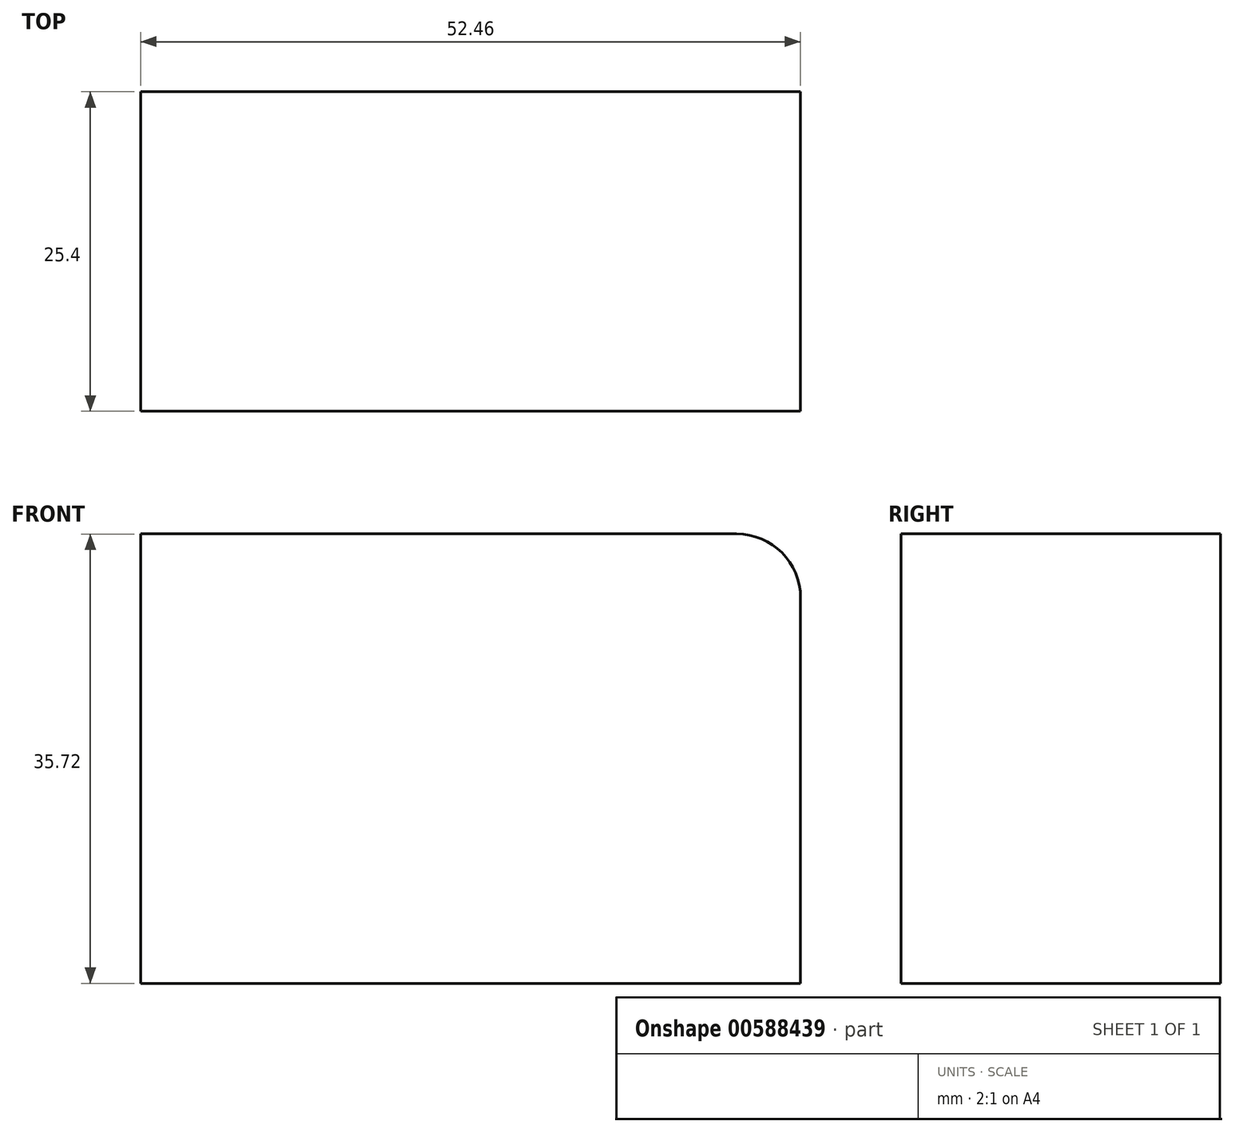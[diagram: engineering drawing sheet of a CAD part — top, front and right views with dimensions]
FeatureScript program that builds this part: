
annotation { "Feature Type Name" : "Feature", "Feature Type Description" : "" }
export const myFeature = defineFeature(function(context is Context, id is Id, definition is map)
    precondition{}
    {
        {
            var Q0;
            Q0=qCreatedBy(makeId("Front.planeOp"),FACE);
            var sketch = newSketch(context, id + "F0", { "sketchPlane" : qUnion([Q0])});
            skLineSegment(sketch, "E0", {"start": v(-61.77, 45.7) * mm, "end": v(-61.77, 9.97) * mm});
            skLineSegment(sketch, "E1", {"start": v(-61.77, 9.97) * mm, "end": v(-9.3, 9.97) * mm});
            skLineSegment(sketch, "E2", {"start": v(-9.3, 9.97) * mm, "end": v(-9.3, 45.7) * mm});
            skLineSegment(sketch, "E3", {"start": v(-9.3, 45.7) * mm, "end": v(-61.77, 45.7) * mm});
            skSolve(sketch);
        }
        {
            var Q0;
            Q0=makeQuery(id+"F0.imprint","IMPRINT",FACE,{"disambiguationData":[TD([[makeQuery(id+"F0.imprint","IMPRINT",EDGE,{"derivedFrom":sQuery(id+"F0.wireOp",EDGE,"E0")}),1.0]])]});
            var sketch = newSketch(context, id + "F1", { "sketchPlane" : qUnion([Q0])});
            skSolve(sketch);
        }
        {
            var Q0;
            Q0 = qSketchRegion(id + "F1", true);
            var Q1;
            Q1=makeQuery(id+"F0.imprint","IMPRINT",FACE,{"disambiguationData":[TD([[makeQuery(id+"F0.imprint","IMPRINT",EDGE,{"derivedFrom":sQuery(id+"F0.wireOp",EDGE,"E0")}),1.0]])]});
            extrude(context, id + "F2", {"entities" : qUnion([Q0, Q1]), "depth" : 25.4 * mm, "offsetDistance" : 25.4 * mm});
        }
        {
            var Q0;
            Q0=makeQuery(id+"F2.opExtrude","SWEPT_EDGE",EDGE,{"disambiguationData":[OSD([sQuery(id+"F0.wireOp",EDGE,"E2"),sQuery(id+"F0.wireOp",EDGE,"E3")])]});
            fillet(context, id + "F3", {"entities" : qUnion([Q0]), "radius" : 5.08 * mm, "tangentPropagation" : true, "allowEdgeOverflow" : false});
        }
    });
